# Revit family: Deca_Bidê com 3 furos_Living_B.34
name_source: partatom
category: Plumbing Fixtures
units: mm (PartAtom-declared; Revit-internal decimal feet)

## family parameters
Cut with Voids When Loaded = No
Host = Face
Part Type = Normal
Room Calculation Point = No
Round Connector Dimension = Use Diameter
Shared = No

## types (2) — shared parameters
Acompanha o Produto = -
Aprovado por = quattroD
Atendimento ao Cliente = 0800-0117073
Categoria = BACIAS E BIDES
Composição Anel Vedação = -
Composição Assento = -
Composição Básica = Argila, feldspato, caulim, vidrados e corantes inorgânicos.
Composição Componente = Não Possui
Consumo = -
Cor Interna = -
Cor Secundária = -
Cores Componente = Não Possui
Criado por = quattroD
Código Pai = B.34
Description = Bidê com 3 furos
Diâmetro Ponto de Esgoto = 40 mm  [stored 0.131234 ft]
Diâmetro Água Fria = 15 mm  [stored 0.0492126 ft]
Diâmetro Água Quente = 15 mm  [stored 0.0492126 ft]
Informações Complementares = -
Itens de Instalação = 1895.C14; 1895.C26; 1895.C33; 1895.C34; 1895.C35; 1895.C37; 1895.C38; 1895.C40.CR; 1895.C43; 1895.C50; 1895.C52; 1895.C64; 1895.C81; 1895.C84; 1895.C86; 1895.C87; 1895.C90; 1895.C94; SP.121.01
Linha = Deca Living
Manufacturer = Deca
Norma = NBR-16728-1;NBR-16728-2
Peso Líquido (Kg) = 28.638
Pressão máx. funcionamento = -
Pressão mín. Aquec. Acúmulo = -
Pressão mín. Aquec. Passagem = -
Pressão mín. funcionamento = -
Raio Ponto de Esgoto = 20 mm  [stored 0.0656168 ft]
Raio Água Fria = 7.5 mm  [stored 0.0246063 ft]
Raio Água Quente = 7.5 mm  [stored 0.0246063 ft]
Saída de Esgoto = Saída de Esgoto Vertical
Segmento = Banheiro Médio
Tipo de dispositivo economizador = -
Tipo de mecanismo utilizado = -
Tipo de rosca de entrada = -
Tipo de rosca de saída = -
URL = www.deca.com.br
Vazão na Pressão máx. (L/min) = -
Vazão na Pressão mín. (L/min) = -
zero-valued in all types: Default Elevation

## per-type parameters (varying)
| type | Cor Principal | Material | Model |
| B.34.17_Branco | Branco | Deca_Branco | B.34.17 |
| B.34.95_Ébano | Ébano | Deca_Ébano | B.34.95 |

note: [stored X ft] marks values corroborated as IEEE doubles in the binary element streams (Revit-internal decimal feet)

## geometry (parser evidence)
native form markers: Sweep x2
no freeform markers — native parametric forms only
